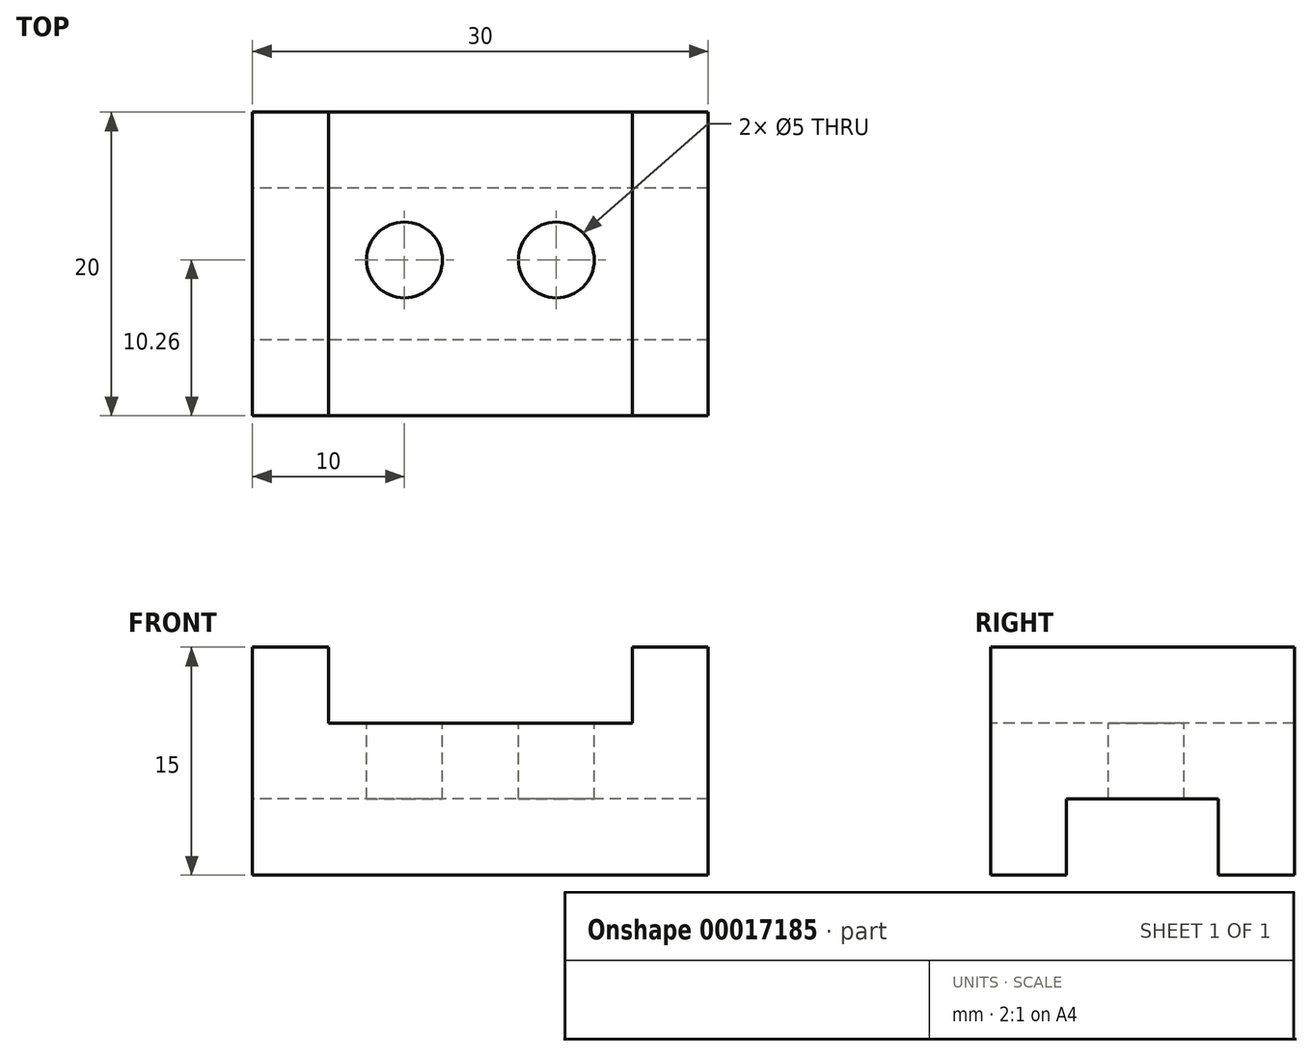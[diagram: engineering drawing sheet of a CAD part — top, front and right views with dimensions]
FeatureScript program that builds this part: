
annotation { "Feature Type Name" : "Feature", "Feature Type Description" : "" }
export const myFeature = defineFeature(function(context is Context, id is Id, definition is map)
    precondition{}
    {
        {
            var Q0;
            Q0=qCreatedBy(makeId("Right.planeOp"),FACE);
            var sketch = newSketch(context, id + "F0", { "sketchPlane" : qUnion([Q0])});
            skLineSegment(sketch, "E0", {"start": v(-5.26, -4.89) * mm, "end": v(-10.26, -4.89) * mm});
            skLineSegment(sketch, "E1", {"start": v(-10.26, -4.89) * mm, "end": v(-10.26, 10.11) * mm});
            skLineSegment(sketch, "E2", {"start": v(-10.26, 10.11) * mm, "end": v(9.74, 10.11) * mm});
            skLineSegment(sketch, "E3", {"start": v(9.74, 10.11) * mm, "end": v(9.74, -4.89) * mm});
            skLineSegment(sketch, "E4", {"start": v(9.74, -4.89) * mm, "end": v(4.74, -4.89) * mm});
            skLineSegment(sketch, "E5", {"start": v(4.74, -4.89) * mm, "end": v(4.74, 0.11) * mm});
            skLineSegment(sketch, "E6", {"start": v(4.74, 0.11) * mm, "end": v(-5.26, 0.11) * mm});
            skLineSegment(sketch, "E7", {"start": v(-5.26, 0.11) * mm, "end": v(-5.26, -4.89) * mm});
            skSolve(sketch);
        }
        {
            var Q0;
            Q0 = qSketchRegion(id + "F0", true);
            extrude(context, id + "F1", {"entities" : qUnion([Q0]), "depth" : 30 * mm});
        }
        {
            var Q0;
            Q0=makeQuery(id+"F1.opExtrude","SWEPT_FACE",FACE,{"disambiguationData":[OSD([sQuery(id+"F0.wireOp",EDGE,"E1")])]});
            var sketch = newSketch(context, id + "F2", { "sketchPlane" : qUnion([Q0])});
            skLineSegment(sketch, "E8", {"start": v(5, 10.11) * mm, "end": v(5, 5.11) * mm});
            skLineSegment(sketch, "E9", {"start": v(5, 5.11) * mm, "end": v(25, 5.11) * mm});
            skLineSegment(sketch, "E10", {"start": v(25, 5.11) * mm, "end": v(25, 10.11) * mm});
            skSolve(sketch);
        }
        {
            var Q0;
            {var subQ2=sQuery(id+"F2.wireOp",EDGE,"E8");Q0=makeQuery(id+"F2.imprint","IMPRINT",FACE,{"disambiguationData":[TD([[makeQuery(id+"F2.imprint","IMPRINT",EDGE,{"derivedFrom":subQ2}),1.0]])]});}
            extrude(context, id + "F3", {"entities" : qUnion([Q0]), "operationType" : NewBodyOperationType.REMOVE, "endBound" : BoundingType.THROUGH_ALL, "oppositeDirection" : true, "depth" : 25 * mm});
        }
        {
            var Q0;
            Q0=makeQuery(id+"F3.boolean.opBoolean","COPY",FACE,{"derivedFrom":makeQuery(id+"F3.opExtrude","SWEPT_FACE",FACE,{"disambiguationData":[OSD([sQuery(id+"F2.wireOp",EDGE,"E9")])]})});
            var sketch = newSketch(context, id + "F4", { "sketchPlane" : qUnion([Q0])});
            skCircle(sketch, "E11", {"center": v(10, 0) * mm, "radius": 2.5 * mm});
            skCircle(sketch, "E12", {"center": v(20, 0) * mm, "radius": 2.5 * mm});
            skSolve(sketch);
        }
        {
            var Q0;
            Q0 = qSketchRegion(id + "F4", true);
            extrude(context, id + "F5", {"entities" : qUnion([Q0]), "operationType" : NewBodyOperationType.REMOVE, "endBound" : BoundingType.THROUGH_ALL, "oppositeDirection" : true, "depth" : 25 * mm});
        }
    });
